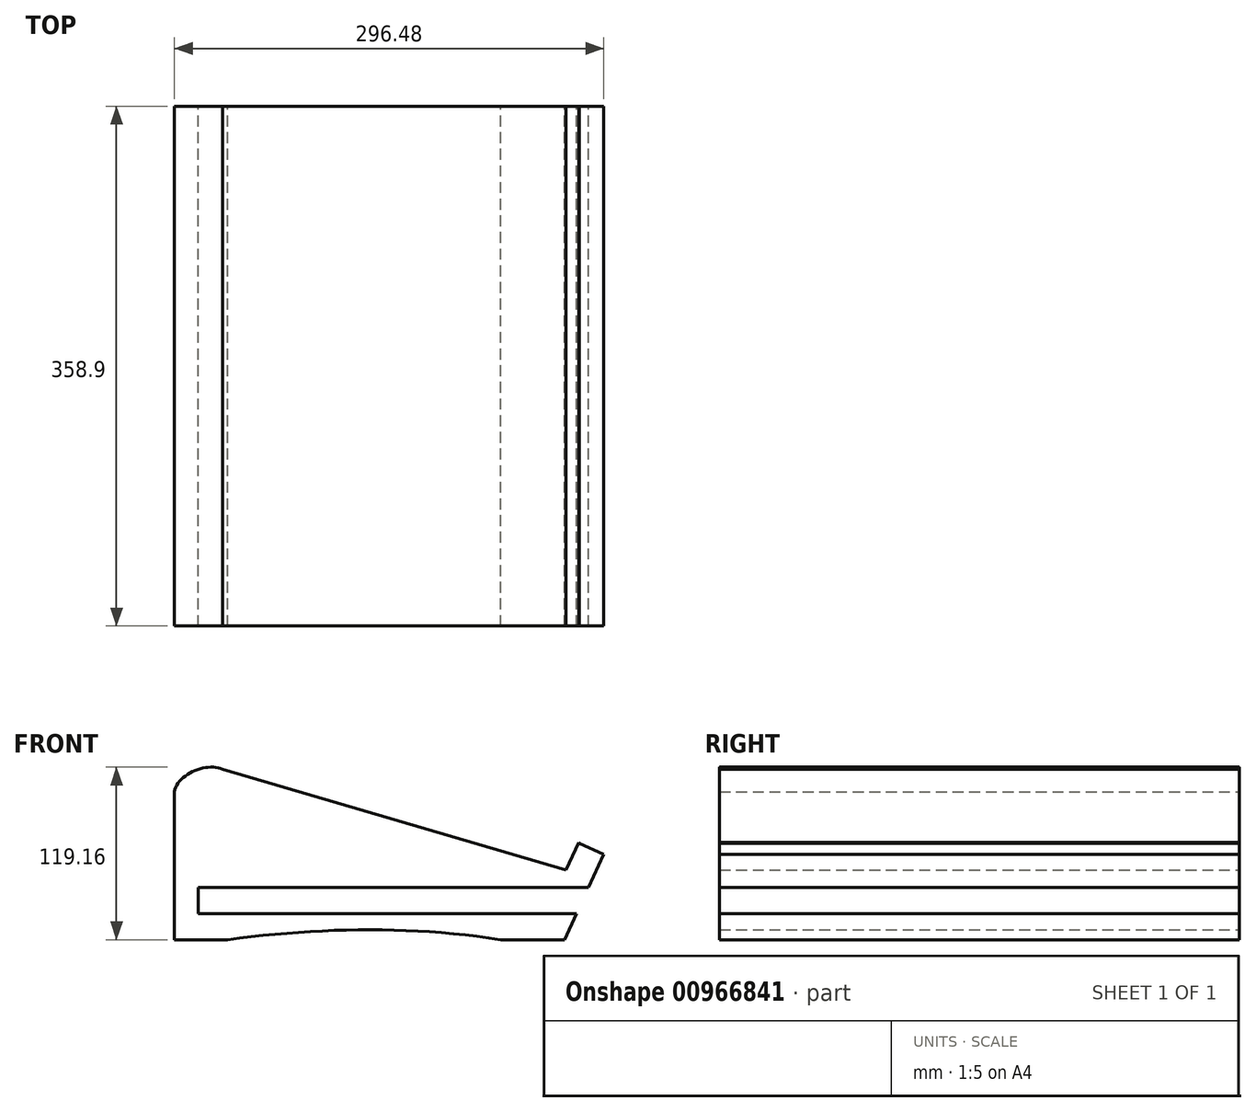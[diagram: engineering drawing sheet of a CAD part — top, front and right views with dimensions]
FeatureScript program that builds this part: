
annotation { "Feature Type Name" : "Feature", "Feature Type Description" : "" }
export const myFeature = defineFeature(function(context is Context, id is Id, definition is map)
    precondition{}
    {
        {
            var Q0;
            Q0=qCreatedBy(makeId("Front.planeOp"),FACE);
            var sketch = newSketch(context, id + "F0", { "sketchPlane" : qUnion([Q0])});
            skLineSegment(sketch, "E0", {"start": v(83.46, 0) * mm, "end": v(127.6, 0) * mm});
            skLineSegment(sketch, "E1", {"start": v(-105.08, 0) * mm, "end": v(-141.76, 0) * mm});
            skLineSegment(sketch, "E2", {"start": v(128.67, 48) * mm, "end": v(137.5, 67.16) * mm});
            skLineSegment(sketch, "E3", {"start": v(154.72, 58.83) * mm, "end": v(127.6, 0) * mm});
            skLineSegment(sketch, "E4", {"start": v(137.87, 67) * mm, "end": v(137.5, 67.16) * mm});
            skLineSegment(sketch, "E5", {"start": v(137.7, 66.59) * mm, "end": v(137.87, 67) * mm});
            skLineSegment(sketch, "E6", {"start": v(137.7, 66.59) * mm, "end": v(154.72, 58.83) * mm});
            skLineSegment(sketch, "E7", {"start": v(-141.76, 0) * mm, "end": v(-141.76, 102.03) * mm});
            skLineSegment(sketch, "E8", {"start": v(144.2, 36) * mm, "end": v(-141.76, 36) * mm});
            skPoint(sketch, "E8.endSnap0", {"position": v(57.45, 36) * mm});
            skPoint(sketch, "E8.endSnap1", {"position": v(-141.76, 51.02) * mm});
            skLineSegment(sketch, "E9", {"start": v(-141.76, 36) * mm, "end": v(-141.76, 18) * mm});
            skLineSegment(sketch, "E10", {"start": v(-141.76, 18) * mm, "end": v(135.9, 18) * mm});
            skLineSegment(sketch, "E11", {"start": v(-125.37, 36) * mm, "end": v(-125.37, 18) * mm});
            skFitSpline(sketch, "E12", {"points": [v(-105.08, 0) * mm, v(83.46, 0) * mm], "startDerivative": vector(186.95, 25.26) * mm, "endDerivative": vector(186.73, -29.37) * mm});
            skLineSegment(sketch, "E13", {"start": v(-108.45, 117.53) * mm, "end": v(128.67, 48) * mm});
            skFitSpline(sketch, "E14", {"points": [v(-141.76, 102.03) * mm, v(-108.45, 117.53) * mm], "startDerivative": vector(5.2, 36.67) * mm, "endDerivative": vector(33.64, -16.13) * mm});
            skSolve(sketch);
        }
        {
            var Q0;
            Q0=makeQuery(id+"F0.imprint","IMPRINT",FACE,{"disambiguationData":[TD([[makeQuery(id+"F0.imprint","IMPRINT",EDGE,{"derivedFrom":sQuery(id+"F0.wireOp",EDGE,"E2")}),-1.0]])]});
            var Q1;
            {var subQ1=sQuery(id+"F0.wireOp",EDGE,"E0");Q1=makeQuery(id+"F0.imprint","IMPRINT",FACE,{"disambiguationData":[TD([[makeQuery(id+"F0.imprint","IMPRINT",EDGE,{"derivedFrom":subQ1}),1.0]])]});}
            var Q2;
            {var subQ5=sQuery(id+"F0.wireOp",EDGE,"E11");Q2=makeQuery(id+"F0.imprint","IMPRINT",FACE,{"disambiguationData":[TD([[makeQuery(id+"F0.imprint","IMPRINT",EDGE,{"derivedFrom":subQ5}),-1.0]])]});}
            extrude(context, id + "F1", {"entities" : qUnion([Q0, Q1, Q2]), "endBound" : BoundingType.SYMMETRIC, "depth" : 358.9 * mm, "offsetDistance" : 25 * mm});
        }
    });
